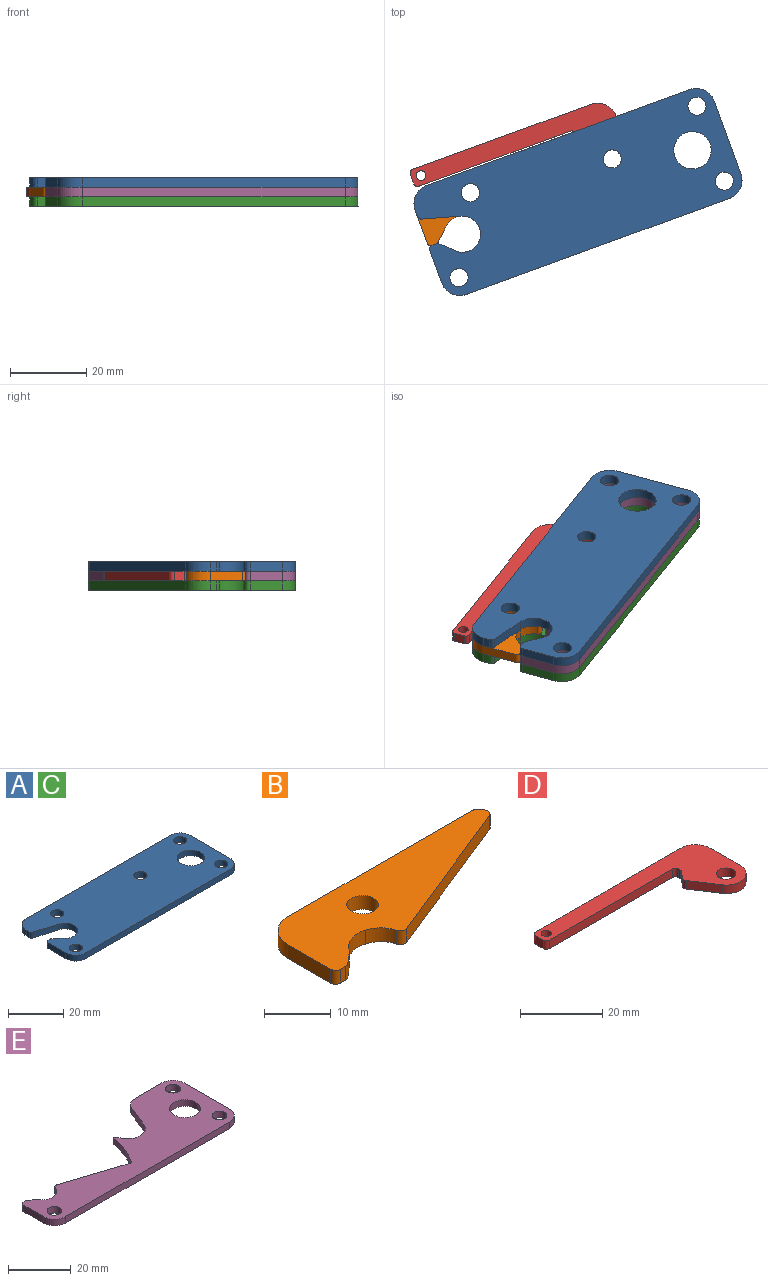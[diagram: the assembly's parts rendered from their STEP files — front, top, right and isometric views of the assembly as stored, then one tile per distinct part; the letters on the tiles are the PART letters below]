
ASSEMBLY  parts=5 mates=4
PART A: 25 faces, bbox 83.8x30.5x2.5 mm
  f0: plane 73.66x2.54mm, normal (0,1,0), area 187.1mm2, adj f15,f16,f19,f20
  f1: plane 2.54x1.77mm, normal (-1,0,0), area 4.5mm2, adj f15,f16,f20,f24
  f2: plane 10.07x2.83mm, normal (-0.27,-0.96,0), area 26.6mm2, adj f3,f15,f16,f24
  f3: cylinder r=4.76mm len=9.35mm, axis (0,0,-1), area 45.2mm2, adj f2,f15,f16,f21
  f4: plane 2.54x1.68mm, normal (0.65,0.76,0), area 5.6mm2, adj f15,f16,f21,f22
  f5: plane 2.54x1.15mm, normal (0,1,0), area 2.9mm2, adj f15,f16,f22,f23
  f6: plane 9.14x2.54mm, normal (-1,0,0), area 23.2mm2, adj f15,f16,f17,f23
  f7: plane 73.66x2.54mm, normal (0,-1,0), area 187.1mm2, adj f15,f16,f17,f18
  f8: cylinder r=2.38mm len=4.76mm, axis (0,0,-1), area 38mm2, adj f15,f16
  f9: cylinder r=4.92mm len=9.84mm, axis (0,0,-1), area 78.5mm2, adj f15,f16
  f10: cylinder r=2.38mm len=4.76mm, axis (0,0,-1), area 38mm2, adj f15,f16
  f11: cylinder r=2.38mm len=4.76mm, axis (0,0,-1), area 38mm2, adj f15,f16
  f12: cylinder r=2.38mm len=4.76mm, axis (0,0,-1), area 38mm2, adj f15,f16
  f13: plane 20.32x2.54mm, normal (1,0,0), area 51.6mm2, adj f15,f16,f18,f19
  f14: cylinder r=2.38mm len=4.76mm, axis (0,0,-1), area 38mm2, adj f15,f16
  f15: plane 83.82x30.48mm, normal (0,0,1), area 2251.3mm2, adj f0,f1,f2,f3,f4,f5,f6,f7
  f16: plane 83.82x30.48mm, normal (0,0,-1), area 2251.3mm2, adj f0,f1,f2,f3,f4,f5,f6,f7
  f17: cylinder r=5.08mm len=5.08mm, axis (0,0,-1), area 20.3mm2, adj f6,f7,f15,f16
  f18: cylinder r=5.08mm len=5.08mm, axis (0,0,-1), area 20.3mm2, adj f7,f13,f15,f16
  f19: cylinder r=5.08mm len=5.08mm, axis (0,0,1), area 20.3mm2, adj f0,f13,f15,f16
  f20: cylinder r=5.08mm len=5.08mm, axis (0,0,1), area 20.3mm2, adj f0,f1,f15,f16
  f21: cylinder r=12.7mm len=2.54mm, axis (0,0,-1), area 5mm2, adj f3,f4,f15,f16
  f22: cylinder r=1.02mm len=2.54mm, axis (0,0,-1), area 1.8mm2, adj f4,f5,f15,f16
  f23: cylinder r=1.02mm len=2.54mm, axis (0,0,1), area 4.1mm2, adj f5,f6,f15,f16
  f24: cylinder r=1.02mm len=2.54mm, axis (0,0,-1), area 3.3mm2, adj f1,f2,f15,f16
PART B: 20 faces, bbox 45.7x15.2x2.5 mm
  f0: plane 9.14x2.54mm, normal (-1,0,0), area 23.2mm2, adj f10,f11,f12,f17
  f1: plane 2.54x1.15mm, normal (0,-1,0), area 2.9mm2, adj f10,f11,f17,f18
  f2: plane 2.54x1.72mm, normal (0.66,-0.76,0), area 5.8mm2, adj f10,f11,f18,f19
  f3: cylinder r=4.77mm len=4.93mm, axis (0,0,-1), area 13.8mm2, adj f4,f10,f11,f19
  f4: cylinder r=4.76mm len=3.4mm, axis (0,0,-1), area 12.7mm2, adj f3,f10,f11,f13
  f5: plane 29.58x11.95mm, normal (0.37,-0.93,0), area 81mm2, adj f10,f11,f13,f14
  f6: plane 2.54x0.16mm, normal (1,0,0), area 0.4mm2, adj f10,f11,f14,f15
  f7: plane 2.54x0.68mm, normal (0.71,0.71,0), area 2.4mm2, adj f10,f11,f15,f16
  f8: plane 38.95x2.54mm, normal (0,1,0), area 98.9mm2, adj f10,f11,f12,f16
  f9: cylinder r=2.38mm len=4.76mm, axis (0,0,-1), area 38mm2, adj f10,f11
  f10: plane 45.72x15.24mm, normal (0,0,1), area 434.1mm2, adj f0,f1,f2,f3,f4,f5,f6,f7
  f11: plane 45.72x15.24mm, normal (0,0,-1), area 434.1mm2, adj f0,f1,f2,f3,f4,f5,f6,f7
  f12: cylinder r=5.08mm len=5.08mm, axis (0,0,1), area 20.3mm2, adj f0,f8,f10,f11
  f13: cylinder r=1.02mm len=2.54mm, axis (0,0,-1), area 4.4mm2, adj f4,f5,f10,f11
  f14: cylinder r=1.02mm len=2.54mm, axis (0,0,-1), area 3.1mm2, adj f5,f6,f10,f11
  f15: cylinder r=1.02mm len=2.54mm, axis (0,0,-1), area 2mm2, adj f6,f7,f10,f11
  f16: cylinder r=1.02mm len=2.54mm, axis (0,0,1), area 2mm2, adj f7,f8,f10,f11
  f17: cylinder r=1.02mm len=2.54mm, axis (0,0,-1), area 4.1mm2, adj f0,f1,f10,f11
  f18: cylinder r=1.02mm len=2.54mm, axis (0,0,-1), area 1.8mm2, adj f1,f2,f10,f11
  f19: cylinder r=12.7mm len=2.54mm, axis (0,0,-1), area 4.8mm2, adj f2,f3,f10,f11
PART C: same geometry as A
PART D: 18 faces, bbox 56.1x20.3x2.5 mm
  f0: plane 2.54x0.88mm, normal (-1,0,0), area 2.2mm2, adj f10,f11,f15,f17
  f1: cylinder r=10.77mm len=2.54mm, axis (0,0,-1), area 6.9mm2, adj f10,f11,f16,f17
  f2: plane 7.51x4.93mm, normal (-0.84,-0.55,0), area 22.8mm2, adj f3,f10,f11,f16
  f3: cylinder r=4.83mm len=8.86mm, axis (0,0,-1), area 31.4mm2, adj f2,f4,f10,f11
  f4: plane 10.35x2.54mm, normal (1,0,0), area 26.3mm2, adj f3,f10,f11,f12
  f5: plane 50.04x2.54mm, normal (0,1,0), area 127.1mm2, adj f10,f11,f12,f13
  f6: plane 2.73x2.54mm, normal (-1,0,0), area 6.9mm2, adj f10,f11,f13,f14
  f7: plane 42.42x2.54mm, normal (0,-1,0), area 107.7mm2, adj f10,f11,f14,f15
  f8: cylinder r=1.27mm len=2.54mm, axis (0,0,-1), area 20.3mm2, adj f10,f11
  f9: cylinder r=2.38mm len=4.76mm, axis (0,0,-1), area 38mm2, adj f10,f11
  f10: plane 56.13x20.26mm, normal (0,0,1), area 408.5mm2, adj f0,f1,f2,f3,f4,f5,f6,f7
  f11: plane 56.13x20.26mm, normal (0,0,-1), area 408.5mm2, adj f0,f1,f2,f3,f4,f5,f6,f7
  f12: cylinder r=5.08mm len=5.08mm, axis (0,0,-1), area 20.3mm2, adj f4,f5,f10,f11
  f13: cylinder r=1.02mm len=2.54mm, axis (0,0,-1), area 4.1mm2, adj f5,f6,f10,f11
  f14: cylinder r=1.02mm len=2.54mm, axis (0,0,-1), area 4.1mm2, adj f6,f7,f10,f11
  f15: cylinder r=1.02mm len=2.54mm, axis (0,0,1), area 4.1mm2, adj f0,f7,f10,f11
  f16: cylinder r=1.02mm len=2.54mm, axis (0,0,-1), area 3mm2, adj f1,f2,f10,f11
  f17: cylinder r=1.02mm len=2.54mm, axis (0,0,-1), area 2.2mm2, adj f0,f1,f10,f11
PART E: 28 faces, bbox 83.8x30.5x2.5 mm
  f0: plane 11.85x2.54mm, normal (0,1,0), area 30.1mm2, adj f18,f19,f20,f23
  f1: plane 8.78x3.55mm, normal (-0.93,0.37,0), area 24mm2, adj f2,f18,f19,f20
  f2: cylinder r=5.59mm len=9.52mm, axis (0,0,-1), area 29.8mm2, adj f1,f3,f18,f19
  f3: plane 3.24x2.54mm, normal (0.84,0.55,0), area 9.8mm2, adj f2,f4,f18,f19
  f4: cylinder r=0.25mm len=2.54mm, axis (0,0,-1), area 1.6mm2, adj f3,f5,f18,f19
  f5: cylinder r=31.68mm len=12.92mm, axis (0,0,-1), area 35.6mm2, adj f4,f6,f18,f19
  f6: cylinder r=1.27mm len=2.54mm, axis (0,0,-1), area 4.1mm2, adj f5,f7,f18,f19
  f7: plane 24.62x8mm, normal (0.31,0.95,0), area 65.8mm2, adj f6,f18,f19,f25
  f8: cylinder r=4.76mm len=8.15mm, axis (0,0,-1), area 25.6mm2, adj f18,f19,f24,f25
  f9: plane 2.54x1.68mm, normal (0.65,0.76,0), area 5.6mm2, adj f18,f19,f24,f26
  f10: plane 2.54x1.15mm, normal (0,1,0), area 2.9mm2, adj f18,f19,f26,f27
  f11: plane 9.14x2.54mm, normal (-1,0,0), area 23.2mm2, adj f18,f19,f21,f27
  f12: plane 73.66x2.54mm, normal (0,-1,0), area 187.1mm2, adj f18,f19,f21,f22
  f13: cylinder r=2.38mm len=4.76mm, axis (0,0,-1), area 38mm2, adj f18,f19
  f14: cylinder r=2.38mm len=4.76mm, axis (0,0,-1), area 38mm2, adj f18,f19
  f15: cylinder r=2.38mm len=4.76mm, axis (0,0,-1), area 38mm2, adj f18,f19
  f16: plane 20.32x2.54mm, normal (1,0,0), area 51.6mm2, adj f18,f19,f22,f23
  f17: cylinder r=4.92mm len=9.84mm, axis (0,0,-1), area 78.5mm2, adj f18,f19
  f18: plane 83.82x30.48mm, normal (0,0,1), area 1307.4mm2, adj f0,f1,f2,f3,f4,f5,f6,f7
  f19: plane 83.82x30.48mm, normal (0,0,-1), area 1307.4mm2, adj f0,f1,f2,f3,f4,f5,f6,f7
  f20: cylinder r=5.08mm len=4.71mm, axis (0,0,-1), area 15.3mm2, adj f0,f1,f18,f19
  f21: cylinder r=5.08mm len=5.08mm, axis (0,0,-1), area 20.3mm2, adj f11,f12,f18,f19
  f22: cylinder r=5.08mm len=5.08mm, axis (0,0,-1), area 20.3mm2, adj f12,f16,f18,f19
  f23: cylinder r=5.08mm len=5.08mm, axis (0,0,1), area 20.3mm2, adj f0,f16,f18,f19
  f24: cylinder r=12.7mm len=2.54mm, axis (0,0,-1), area 5mm2, adj f8,f9,f18,f19
  f25: cylinder r=1.02mm len=2.54mm, axis (0,0,-1), area 4mm2, adj f7,f8,f18,f19
  f26: cylinder r=1.02mm len=2.54mm, axis (0,0,-1), area 1.8mm2, adj f9,f10,f18,f19
  f27: cylinder r=1.02mm len=2.54mm, axis (0,0,1), area 4.1mm2, adj f10,f11,f18,f19
PLACE A rot(axis=(0,0,1),20deg) t=(27.39,5.16,0.09)mm
PLACE B rot(axis=(0,0,1),20deg) t=(27.39,5.16,15.33)mm
PLACE C rot(axis=(0,0,1),20deg) t=(27.39,5.16,-4.99)mm
PLACE D rot(axis=(0,0,1),20deg) t=(27.39,5.16,7.71)mm
PLACE E rot(axis=(0,0,1),20deg) t=(27.39,5.16,20.41)mm
MATE revolute B.f9 <-> C.f14  axis (0,0,1) through (33.22,33.65,22.95)mm
MATE fastened E.f15 <-> C.f12  axis (0,0,1) through (30.23,11.27,22.95)mm
MATE revolute D.f1 <-> C.f8  axis (0,0,1) through (70.54,42.53,22.95)mm
MATE fastened C.f12 <-> A.f12  axis (0,0,1) through (30.23,11.27,20.41)mm
